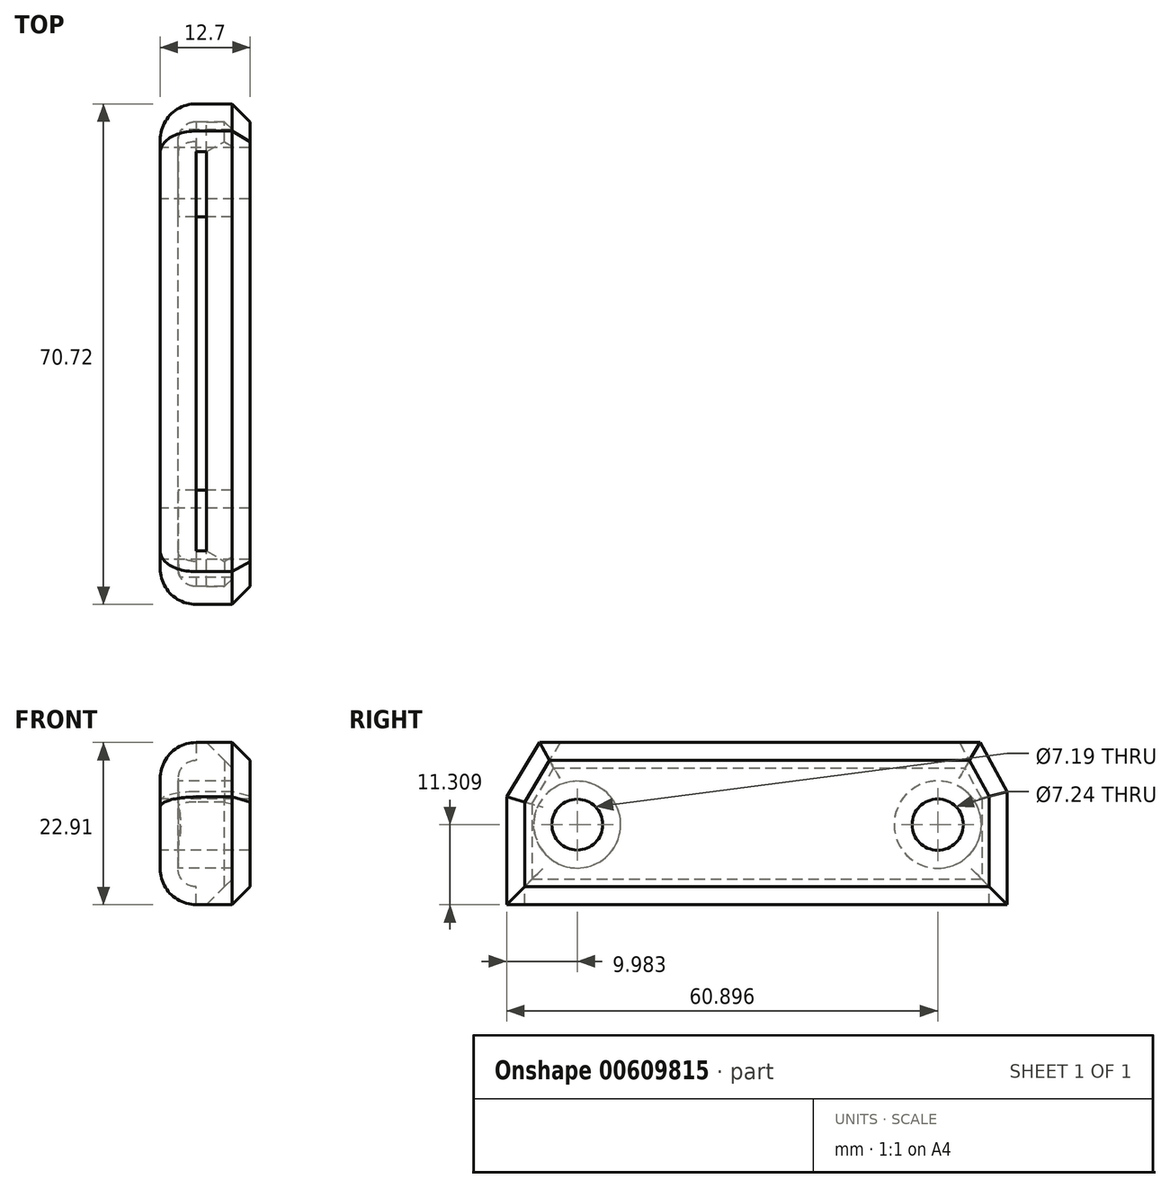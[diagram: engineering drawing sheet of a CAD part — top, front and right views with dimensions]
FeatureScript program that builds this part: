
annotation { "Feature Type Name" : "Feature", "Feature Type Description" : "" }
export const myFeature = defineFeature(function(context is Context, id is Id, definition is map)
    precondition{}
    {
        {
            var Q0;
            Q0=qCreatedBy(makeId("Right.planeOp"),FACE);
            var sketch = newSketch(context, id + "F0", { "sketchPlane" : qUnion([Q0])});
            skLineSegment(sketch, "E0", {"start": v(-38.7, 38.82) * mm, "end": v(-38.7, 23.6) * mm});
            skLineSegment(sketch, "E1", {"start": v(32.02, 39.55) * mm, "end": v(32.02, 23.6) * mm});
            skLineSegment(sketch, "E2", {"start": v(32.02, 23.6) * mm, "end": v(-38.7, 23.6) * mm});
            skLineSegment(sketch, "E3", {"start": v(-38.7, 38.82) * mm, "end": v(-34.07, 46.5) * mm});
            skLineSegment(sketch, "E4", {"start": v(32.02, 39.55) * mm, "end": v(28.17, 46.5) * mm});
            skLineSegment(sketch, "E5", {"start": v(-34.07, 46.5) * mm, "end": v(28.17, 46.5) * mm});
            skCircle(sketch, "E6", {"center": v(-28.72, 34.9) * mm, "radius": 3.6 * mm});
            skCircle(sketch, "E7", {"center": v(22.2, 34.9) * mm, "radius": 3.62 * mm});
            skSolve(sketch);
        }
        {
            var Q0;
            Q0 = qSketchRegion(id + "F0", true);
            extrude(context, id + "F1", {"entities" : qUnion([Q0]), "depth" : 12.7 * mm, "offsetDistance" : 25.4 * mm});
        }
        {
            var Q0;
            Q0=makeQuery(id+"F1.opExtrude","CAP_EDGE",EDGE,{"disambiguationData":[OSD([sQuery(id+"F0.wireOp",EDGE,"E0")])],"isStart":false});
            var Q1;
            Q1=makeQuery(id+"F1.opExtrude","CAP_EDGE",EDGE,{"disambiguationData":[OSD([sQuery(id+"F0.wireOp",EDGE,"E2")])],"isStart":false});
            var Q2;
            Q2=makeQuery(id+"F1.opExtrude","CAP_EDGE",EDGE,{"disambiguationData":[OSD([sQuery(id+"F0.wireOp",EDGE,"E1")])],"isStart":false});
            var Q3;
            Q3=makeQuery(id+"F1.opExtrude","CAP_EDGE",EDGE,{"disambiguationData":[OSD([sQuery(id+"F0.wireOp",EDGE,"E5")])],"isStart":false});
            var Q4;
            Q4=makeQuery(id+"F1.opExtrude","CAP_EDGE",EDGE,{"disambiguationData":[OSD([sQuery(id+"F0.wireOp",EDGE,"E4")])],"isStart":false});
            var Q5;
            Q5=makeQuery(id+"F1.opExtrude","CAP_EDGE",EDGE,{"disambiguationData":[OSD([sQuery(id+"F0.wireOp",EDGE,"E3")])],"isStart":false});
            chamfer(context, id + "F2", {"entities" : qUnion([Q0, Q1, Q2, Q3, Q4, Q5]), "width" : 2.54 * mm, "tangentPropagation" : true});
        }
        {
            var Q0;
            Q0=makeQuery(id+"F1.opExtrude","CAP_EDGE",EDGE,{"disambiguationData":[OSD([sQuery(id+"F0.wireOp",EDGE,"E5")])],"isStart":true});
            var Q1;
            Q1=makeQuery(id+"F1.opExtrude","CAP_EDGE",EDGE,{"disambiguationData":[OSD([sQuery(id+"F0.wireOp",EDGE,"E1")])],"isStart":true});
            var Q2;
            Q2=makeQuery(id+"F1.opExtrude","CAP_EDGE",EDGE,{"disambiguationData":[OSD([sQuery(id+"F0.wireOp",EDGE,"E2")])],"isStart":true});
            var Q3;
            Q3=makeQuery(id+"F1.opExtrude","CAP_EDGE",EDGE,{"disambiguationData":[OSD([sQuery(id+"F0.wireOp",EDGE,"E0")])],"isStart":true});
            var Q4;
            Q4=makeQuery(id+"F1.opExtrude","CAP_EDGE",EDGE,{"disambiguationData":[OSD([sQuery(id+"F0.wireOp",EDGE,"E3")])],"isStart":true});
            var Q5;
            Q5=makeQuery(id+"F1.opExtrude","CAP_EDGE",EDGE,{"disambiguationData":[OSD([sQuery(id+"F0.wireOp",EDGE,"E4")])],"isStart":true});
            fillet(context, id + "F3", {"entities" : qUnion([Q0, Q1, Q2, Q3, Q4, Q5]), "radius" : 5.08 * mm, "tangentPropagation" : true, "allowEdgeOverflow" : false});
        }
        {
            var Q0;
            Q0=makeQuery(id+"F1.opExtrude","SWEPT_FACE",FACE,{"disambiguationData":[OSD([sQuery(id+"F0.wireOp",EDGE,"E2")])]});
            var Q1;
            Q1=makeQuery(id+"F1.opExtrude","SWEPT_FACE",FACE,{"disambiguationData":[OSD([sQuery(id+"F0.wireOp",EDGE,"E5")])]});
            shell(context, id + "F4", {"entities" : qUnion([Q0, Q1]), "thickness" : 2.54 * mm});
        }
    });
